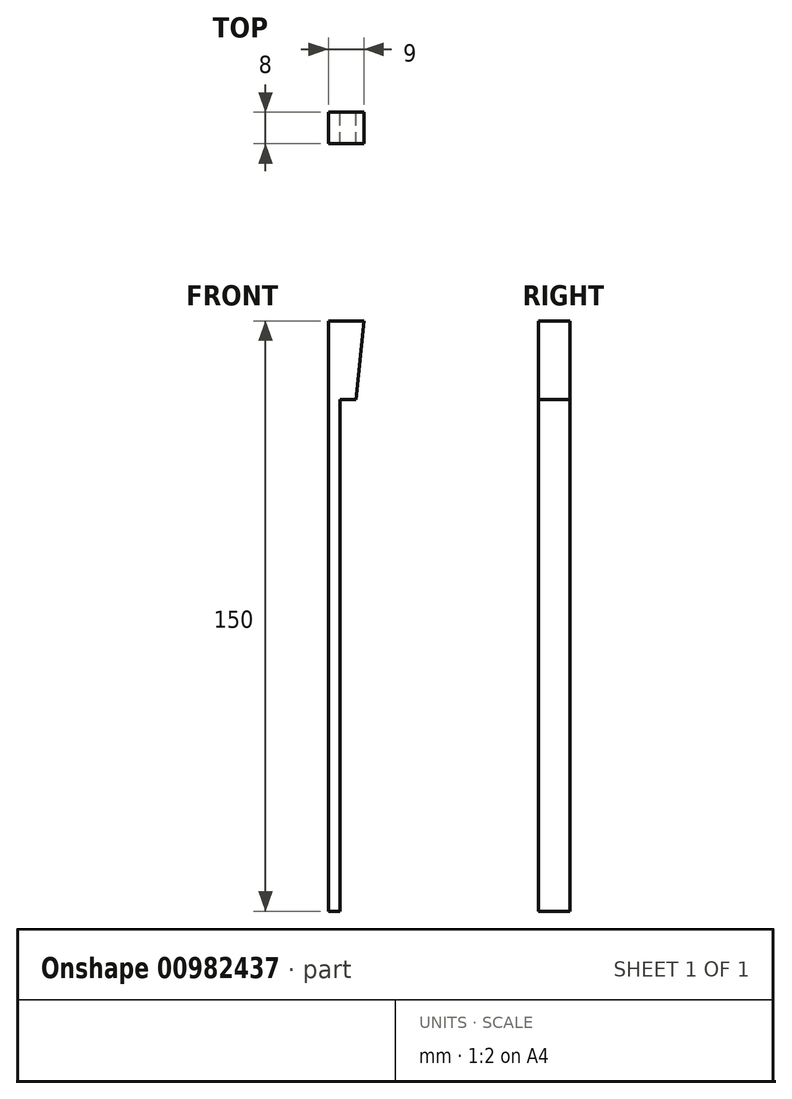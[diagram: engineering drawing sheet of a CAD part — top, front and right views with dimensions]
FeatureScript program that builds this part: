
annotation { "Feature Type Name" : "Feature", "Feature Type Description" : "" }
export const myFeature = defineFeature(function(context is Context, id is Id, definition is map)
    precondition{}
    {
        {
            var Q0;
            Q0=qCreatedBy(makeId("Front.planeOp"),FACE);
            var sketch = newSketch(context, id + "F0", { "sketchPlane" : qUnion([Q0])});
            skLineSegment(sketch, "E0", {"start": v(0, 0) * mm, "end": v(-1.5, 0) * mm, "construction": true});
            skLineSegment(sketch, "E1", {"start": v(-1.5, 0) * mm, "end": v(-1.5, -75) * mm});
            skLineSegment(sketch, "E2", {"start": v(-1.5, -75) * mm, "end": v(1.5, -75) * mm});
            skLineSegment(sketch, "E3", {"start": v(1.5, -75) * mm, "end": v(1.5, 55) * mm});
            skLineSegment(sketch, "E4", {"start": v(1.5, 55) * mm, "end": v(7.5, 55) * mm});
            skLineSegment(sketch, "E5", {"start": v(7.5, 55) * mm, "end": v(7.5, 75) * mm});
            skLineSegment(sketch, "E6", {"start": v(7.5, 75) * mm, "end": v(-1.5, 75) * mm});
            skLineSegment(sketch, "E7", {"start": v(-1.5, 75) * mm, "end": v(-1.5, 0) * mm});
            skLineSegment(sketch, "E8", {"start": v(7.5, 55) * mm, "end": v(5.5, 55) * mm});
            skLineSegment(sketch, "E9", {"start": v(5.5, 55) * mm, "end": v(7.5, 75) * mm});
            skSolve(sketch);
        }
        {
            var Q0;
            Q0=makeQuery(id+"F0.imprint","IMPRINT",FACE,{"disambiguationData":[TD([[makeQuery(id+"F0.imprint","IMPRINT",EDGE,{"derivedFrom":sQuery(id+"F0.wireOp",EDGE,"E1")}),1.0]])]});
            extrude(context, id + "F1", {"entities" : qUnion([Q0]), "depth" : 8 * mm, "offsetDistance" : 25 * mm});
        }
    });
